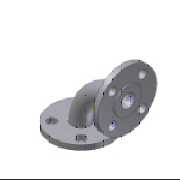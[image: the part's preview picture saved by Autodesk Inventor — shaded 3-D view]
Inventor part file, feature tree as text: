
AUTODESK INVENTOR PART (.ipt)
format: ipt  version: 2023.2 (Build 272271030, 271C)  size: 311,296 bytes
history: native  units: mm (DEFAULTED — no unit token found)
features: sketch x5, other x4, revolve x2, extrude x2, pattern_circular x2, sweep x1
ambient origin geometry x8: Origin, YZ Plane, XZ Plane, XY Plane, X Axis, Y Axis, Z Axis, Center Point
bodies: Solid1 (feature_tree)
feature tree (16):
  sketch  "Sketch1"  dims[d0=438.0mm d1=635.0mm]
  revolve  "Revolution1"  [1 undecoded]
  revolve  "Revolution2"  [1 undecoded]
  sweep  "Sweep1"
  extrude  "Extrusion1"  Depth=40.0mm
  pattern_circular  "Circular Pattern1"  [2 undecoded]
  extrude  "Extrusion2"  Depth=635.0mm
  pattern_circular  "Circular Pattern2"  [2 undecoded]
  other  "Work Point1"
  other  "Work Point2"
  other  "Work Axis1"
  other  "Work Axis2"
  sketch  "Sketch2"  dims[d2=533.5mm d3=2.0mm]
  sketch  "Sketch3"  dims[d4=40.0mm d5=90.0deg]
  sketch  "Sketch6"  dims[d6=2.0mm d7=40.0mm]
  sketch  "Sketch7"  dims[d8=438.0mm d9=533.5mm d10=635.0mm d11=419.0mm d12=419.0mm d13=90.0deg d14=461.8mm d15=0.0mm d16=160.0mm d17=360.0deg d18=160.0mm d19=360.0deg d20=1.963495mm d21=32.5mm d22=578.0mm d34=25.4mm d24=0.0mm d25=1.963495mm d26=32.5mm d27=578.0mm d39=25.4mm d28=0.0mm d41=0.0mm]
note: 6 required parameter values undecoded (feature->parameter linkage not recoverable at this tier; creation-order binding heuristic only, values carry confidence <= 0.55)